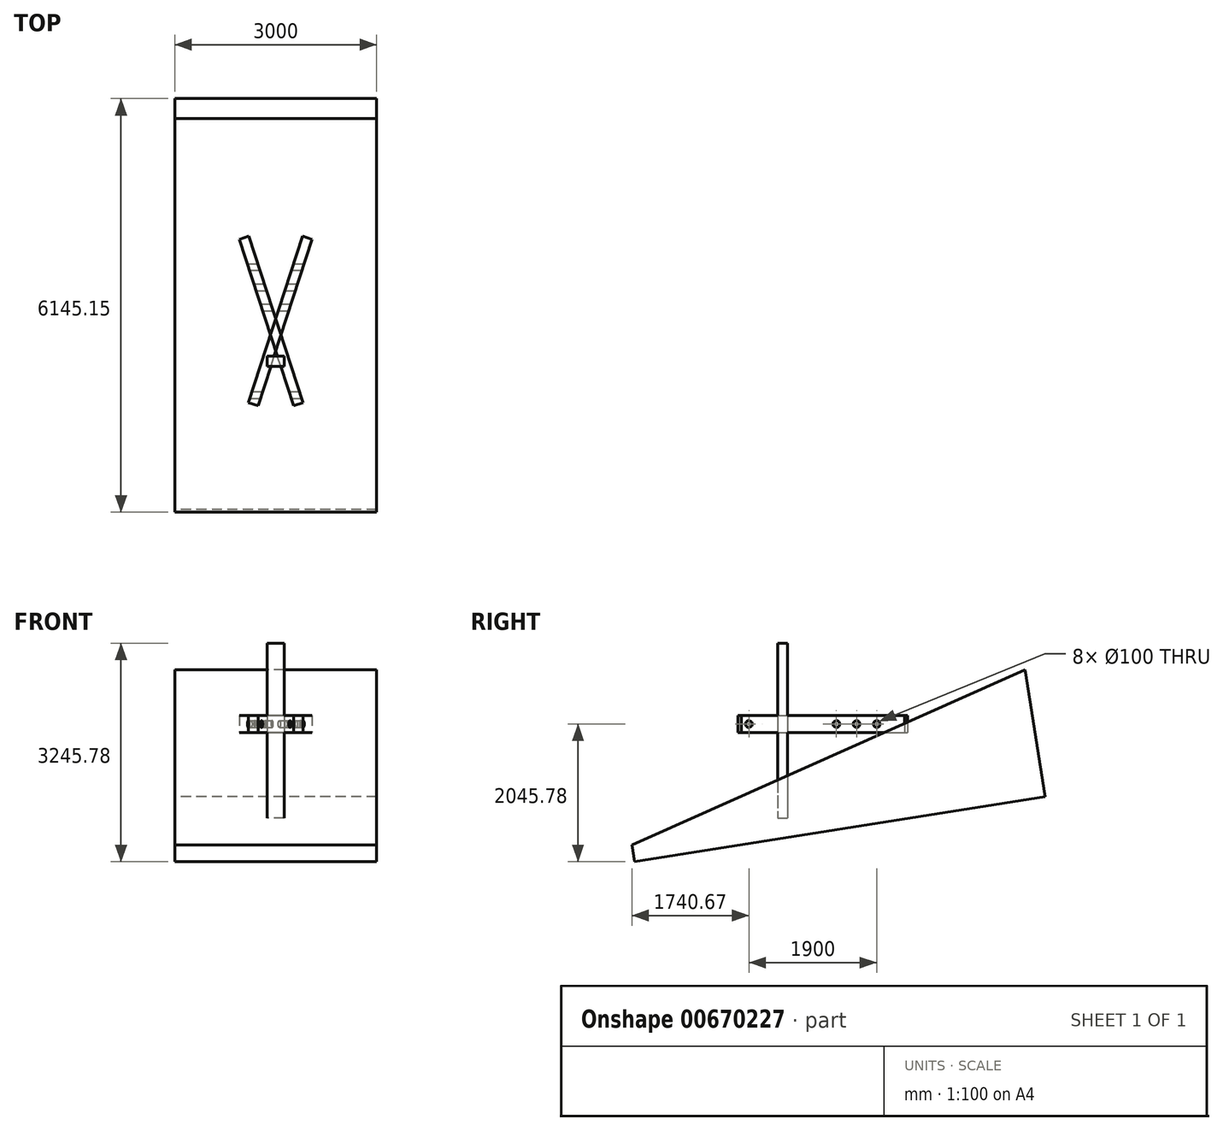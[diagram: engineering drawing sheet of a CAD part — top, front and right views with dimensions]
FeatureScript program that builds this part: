
annotation { "Feature Type Name" : "Feature", "Feature Type Description" : "" }
export const myFeature = defineFeature(function(context is Context, id is Id, definition is map)
    precondition{}
    {
        {
            var Q0;
            Q0=qCreatedBy(makeId("Top.planeOp"),FACE);
            var sketch = newSketch(context, id + "F0", { "sketchPlane" : qUnion([Q0])});
            skLineSegment(sketch, "E0.bottom", {"start": v(125, -75) * mm, "end": v(-125, -75) * mm});
            skLineSegment(sketch, "E0.top", {"start": v(125, 75) * mm, "end": v(-125, 75) * mm});
            skLineSegment(sketch, "E0.left", {"start": v(125, -75) * mm, "end": v(125, 75) * mm});
            skLineSegment(sketch, "E0.right", {"start": v(-125, -75) * mm, "end": v(-125, 75) * mm});
            skPoint(sketch, "E0.middle", {"position": v(0, 0) * mm});
            skSolve(sketch);
        }
        {
            var Q0;
            Q0=makeQuery(id+"F0.imprint","IMPRINT",FACE,{"disambiguationData":[TD([[makeQuery(id+"F0.imprint","IMPRINT",EDGE,{"derivedFrom":sQuery(id+"F0.wireOp",EDGE,"E0.bottom")}),-1.0]])]});
            extrude(context, id + "F1", {"entities" : qUnion([Q0]), "depth" : 2000 * mm, "offsetDistance" : 25 * mm, "hasSecondDirection" : true, "secondDirectionOppositeDirection" : true, "secondDirectionDepth" : 600 * mm});
        }
        {
            var Q0;
            Q0=qCreatedBy(makeId("Right.planeOp"),FACE);
            var sketch = newSketch(context, id + "F2", { "sketchPlane" : qUnion([Q0])});
            skLineSegment(sketch, "E1", {"start": v(-2240.67, -997.61) * mm, "end": v(3606.05, 1605.52) * mm});
            skLineSegment(sketch, "E2", {"start": v(0, 0) * mm, "end": v(503.9, 0) * mm, "construction": true});
            skLineSegment(sketch, "E3", {"start": v(0, 800) * mm, "end": v(1796.83, 800) * mm});
            skLineSegment(sketch, "E4", {"start": v(-2201.37, -1245.78) * mm, "end": v(-2240.67, -997.61) * mm});
            skLineSegment(sketch, "E5", {"start": v(-2201.37, -1245.78) * mm, "end": v(3904.48, -278.71) * mm});
            skLineSegment(sketch, "E6", {"start": v(3904.48, -278.71) * mm, "end": v(3606.05, 1605.52) * mm});
            skSolve(sketch);
        }
        {
            var Q0;
            Q0=sQuery(id+"F2.wireOp",EDGE,"E3");
            var Q1;
            Q1=qCreatedBy(makeId("Right.planeOp"),FACE);
            cPlane(context, id + "F3", {"entities" : qUnion([Q0, Q1]), "cplaneType" : CPlaneType.LINE_ANGLE, "offset" : 25 * mm, "angle" : 90 * degree, "width" : 150 * mm, "height" : 150 * mm});
        }
        {
            var Q0;
            Q0=qCreatedBy(id+"F3.planeOp",FACE);
            var sketch = newSketch(context, id + "F4", { "sketchPlane" : qUnion([Q0])});
            skLineSegment(sketch, "E7", {"start": v(125, 75) * mm, "end": v(125, -75) * mm, "construction": true});
            skLineSegment(sketch, "E8", {"start": v(-125, 75) * mm, "end": v(125, 75) * mm, "construction": true});
            skLineSegment(sketch, "E9", {"start": v(-125, -75) * mm, "end": v(125, -75) * mm, "construction": true});
            skLineSegment(sketch, "E10", {"start": v(-125, 75) * mm, "end": v(-125, -75) * mm, "construction": true});
            skLineSegment(sketch, "E11.bottom", {"start": v(-262.86, -661.08) * mm, "end": v(-405.52, -614.73) * mm});
            skLineSegment(sketch, "E11.top", {"start": v(540.59, 1811.66) * mm, "end": v(397.93, 1858.01) * mm});
            skLineSegment(sketch, "E11.left", {"start": v(-262.86, -661.08) * mm, "end": v(540.59, 1811.66) * mm});
            skLineSegment(sketch, "E11.right", {"start": v(-405.52, -614.73) * mm, "end": v(397.93, 1858.01) * mm});
            skLineSegment(sketch, "E12.MirrorCS", {"start": v(405.52, -614.73) * mm, "end": v(-397.93, 1858.01) * mm});
            skLineSegment(sketch, "E13.MirrorCS", {"start": v(-540.59, 1811.66) * mm, "end": v(-397.93, 1858.01) * mm});
            skLineSegment(sketch, "E14.MirrorCS", {"start": v(262.86, -661.08) * mm, "end": v(405.52, -614.73) * mm});
            skLineSegment(sketch, "E15.MirrorCS", {"start": v(262.86, -661.08) * mm, "end": v(-540.59, 1811.66) * mm});
            skLineSegment(sketch, "E16", {"start": v(-360.11, -475) * mm, "end": v(360.11, -475) * mm, "construction": true});
            skSolve(sketch);
        }
        {
            var Q0;
            {var subQ0=sQuery(id+"F4.wireOp",EDGE,"E11.bottom");Q0=makeQuery(id+"F4.imprint","IMPRINT",FACE,{"disambiguationData":[TD([[makeQuery(id+"F4.imprint","IMPRINT",EDGE,{"derivedFrom":subQ0}),-1.0]])]});}
            var Q1;
            {var subQ0=sQuery(id+"F4.wireOp",EDGE,"E15.MirrorCS");var subQ1=sQuery(id+"F4.wireOp",EDGE,"E11.left");var subQ2=makeQuery(id+"F4.imprint","INTERSECT",VERTEX,{"derivedFrom":[subQ1,subQ0]});Q1=makeQuery(id+"F4.imprint","IMPRINT",FACE,{"disambiguationData":[TD([[makeQuery(id+"F4.imprint","IMPRINT",EDGE,{"disambiguationData":[TD([[subQ2,-1.0]])],"derivedFrom":subQ1}),1.0]])]});}
            var Q2;
            {var subQ0=sQuery(id+"F4.wireOp",EDGE,"E11.top");Q2=makeQuery(id+"F4.imprint","IMPRINT",FACE,{"disambiguationData":[TD([[makeQuery(id+"F4.imprint","IMPRINT",EDGE,{"derivedFrom":subQ0}),1.0]])]});}
            extrude(context, id + "F5", {"entities" : qUnion([Q0, Q1, Q2]), "endBound" : BoundingType.SYMMETRIC, "depth" : 250 * mm, "offsetDistance" : 25 * mm});
        }
        {
            var Q0;
            {var subQ5=sQuery(id+"F4.wireOp",EDGE,"E14.MirrorCS");Q0=makeQuery(id+"F4.imprint","IMPRINT",FACE,{"disambiguationData":[TD([[makeQuery(id+"F4.imprint","IMPRINT",EDGE,{"derivedFrom":subQ5}),1.0]])]});}
            var Q1;
            {var subQ5=sQuery(id+"F4.wireOp",EDGE,"E13.MirrorCS");Q1=makeQuery(id+"F4.imprint","IMPRINT",FACE,{"disambiguationData":[TD([[makeQuery(id+"F4.imprint","IMPRINT",EDGE,{"derivedFrom":subQ5}),-1.0]])]});}
            var Q2;
            {var subQ0=sQuery(id+"F4.wireOp",EDGE,"E15.MirrorCS");var subQ1=sQuery(id+"F4.wireOp",EDGE,"E11.left");var subQ2=makeQuery(id+"F4.imprint","INTERSECT",VERTEX,{"derivedFrom":[subQ1,subQ0]});Q2=makeQuery(id+"F4.imprint","IMPRINT",FACE,{"disambiguationData":[TD([[makeQuery(id+"F4.imprint","IMPRINT",EDGE,{"disambiguationData":[TD([[subQ2,-1.0]])],"derivedFrom":subQ1}),1.0]])]});}
            extrude(context, id + "F6", {"entities" : qUnion([Q0, Q1, Q2]), "endBound" : BoundingType.SYMMETRIC, "depth" : 250 * mm, "offsetDistance" : 25 * mm});
        }
        {
            var Q0;
            Q0 = qSketchRegion(id + "F2", true);
            extrude(context, id + "F7", {"entities" : qUnion([Q0]), "endBound" : BoundingType.SYMMETRIC, "depth" : 3000 * mm, "offsetDistance" : 25 * mm});
        }
        {
            var Q0;
            Q0=qCreatedBy(makeId("Right.planeOp"),FACE);
            var sketch = newSketch(context, id + "F8", { "sketchPlane" : qUnion([Q0])});
            skLineSegment(sketch, "E17", {"start": v(-884.38, 800) * mm, "end": v(2070.08, 800) * mm, "construction": true});
            skLineSegment(sketch, "E18", {"start": v(0, -593.78) * mm, "end": v(0, 1588.67) * mm, "construction": true});
            skCircle(sketch, "E19", {"center": v(-500, 800) * mm, "radius": 50 * mm});
            skCircle(sketch, "E20", {"center": v(800, 800) * mm, "radius": 50 * mm});
            skCircle(sketch, "E21", {"center": v(1100, 800) * mm, "radius": 50 * mm});
            skCircle(sketch, "E22", {"center": v(1400, 800) * mm, "radius": 50 * mm});
            skSolve(sketch);
        }
        {
            var Q0;
            Q0=makeQuery(id+"F8.imprint","IMPRINT",FACE,{"disambiguationData":[TD([[makeQuery(id+"F8.imprint","IMPRINT",EDGE,{"derivedFrom":sQuery(id+"F8.wireOp",EDGE,"E19")}),1.0]])]});
            var Q1;
            Q1=makeQuery(id+"F8.imprint","IMPRINT",FACE,{"disambiguationData":[TD([[makeQuery(id+"F8.imprint","IMPRINT",EDGE,{"derivedFrom":sQuery(id+"F8.wireOp",EDGE,"E20")}),1.0]])]});
            var Q2;
            Q2=makeQuery(id+"F8.imprint","IMPRINT",FACE,{"disambiguationData":[TD([[makeQuery(id+"F8.imprint","IMPRINT",EDGE,{"derivedFrom":sQuery(id+"F8.wireOp",EDGE,"E21")}),1.0]])]});
            var Q3;
            Q3=makeQuery(id+"F8.imprint","IMPRINT",FACE,{"disambiguationData":[TD([[makeQuery(id+"F8.imprint","IMPRINT",EDGE,{"derivedFrom":sQuery(id+"F8.wireOp",EDGE,"E22")}),1.0]])]});
            extrude(context, id + "F9", {"entities" : qUnion([Q0, Q1, Q2, Q3]), "operationType" : NewBodyOperationType.REMOVE, "endBound" : BoundingType.THROUGH_ALL, "oppositeDirection" : true, "depth" : 25 * mm, "offsetDistance" : 25 * mm, "hasSecondDirection" : true, "secondDirectionBound" : SecondDirectionBoundingType.THROUGH_ALL, "secondDirectionOppositeDirection" : false, "secondDirectionDepth" : 25 * mm});
        }
    });
